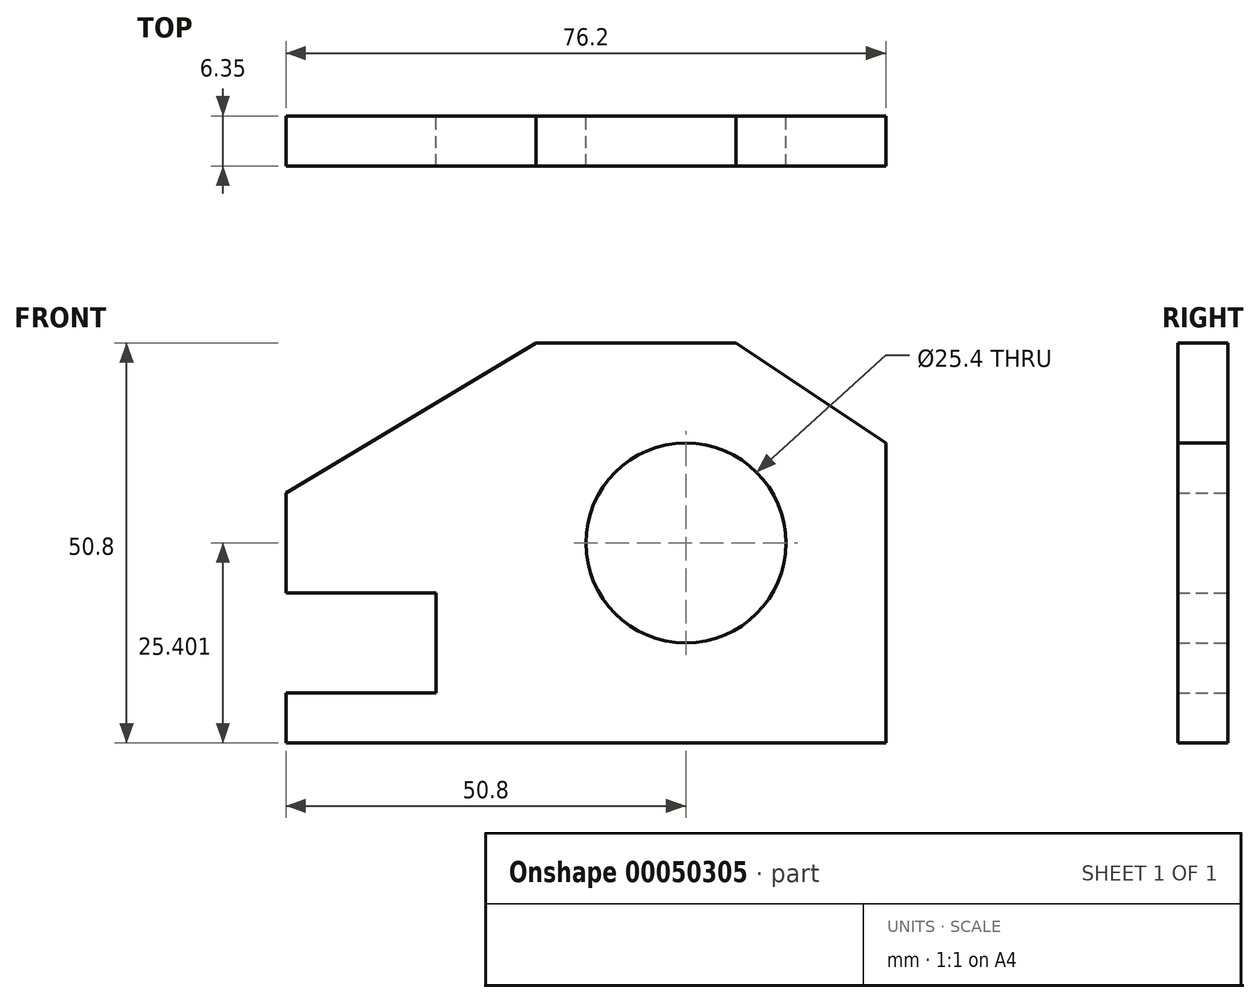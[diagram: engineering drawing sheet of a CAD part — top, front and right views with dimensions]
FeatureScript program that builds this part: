
annotation { "Feature Type Name" : "Feature", "Feature Type Description" : "" }
export const myFeature = defineFeature(function(context is Context, id is Id, definition is map)
    precondition{}
    {
        {
            var Q0;
            Q0=qCreatedBy(makeId("Front.planeOp"),FACE);
            var sketch = newSketch(context, id + "F0", { "sketchPlane" : qUnion([Q0])});
            skLineSegment(sketch, "E0", {"start": v(-57.15, -34.18) * mm, "end": v(19.05, -34.18) * mm});
            skLineSegment(sketch, "E1", {"start": v(-57.15, -34.18) * mm, "end": v(-57.15, -27.83) * mm});
            skLineSegment(sketch, "E2", {"start": v(-57.15, -27.83) * mm, "end": v(-38.1, -27.83) * mm});
            skLineSegment(sketch, "E3", {"start": v(-38.1, -27.83) * mm, "end": v(-38.1, -15.13) * mm});
            skLineSegment(sketch, "E4", {"start": v(-38.1, -15.13) * mm, "end": v(-57.15, -15.13) * mm});
            skLineSegment(sketch, "E5", {"start": v(-57.15, -15.13) * mm, "end": v(-57.15, -2.43) * mm});
            skLineSegment(sketch, "E6", {"start": v(19.05, -34.18) * mm, "end": v(19.05, 3.92) * mm});
            skLineSegment(sketch, "E7", {"start": v(19.05, 3.92) * mm, "end": v(0, 16.62) * mm});
            skLineSegment(sketch, "E8", {"start": v(0, 16.62) * mm, "end": v(-25.4, 16.62) * mm});
            skLineSegment(sketch, "E9", {"start": v(-57.15, -2.43) * mm, "end": v(-25.4, 16.62) * mm});
            skCircle(sketch, "E10", {"center": v(-6.35, -8.78) * mm, "radius": 12.7 * mm});
            skSolve(sketch);
        }
        {
            var Q0;
            Q0=makeQuery(id+"F0.imprint","IMPRINT",FACE,{"disambiguationData":[TD([[makeQuery(id+"F0.imprint","IMPRINT",EDGE,{"derivedFrom":sQuery(id+"F0.wireOp",EDGE,"E0")}),1.0]])]});
            extrude(context, id + "F1", {"entities" : qUnion([Q0]), "depth" : 6.35 * mm});
        }
    });
